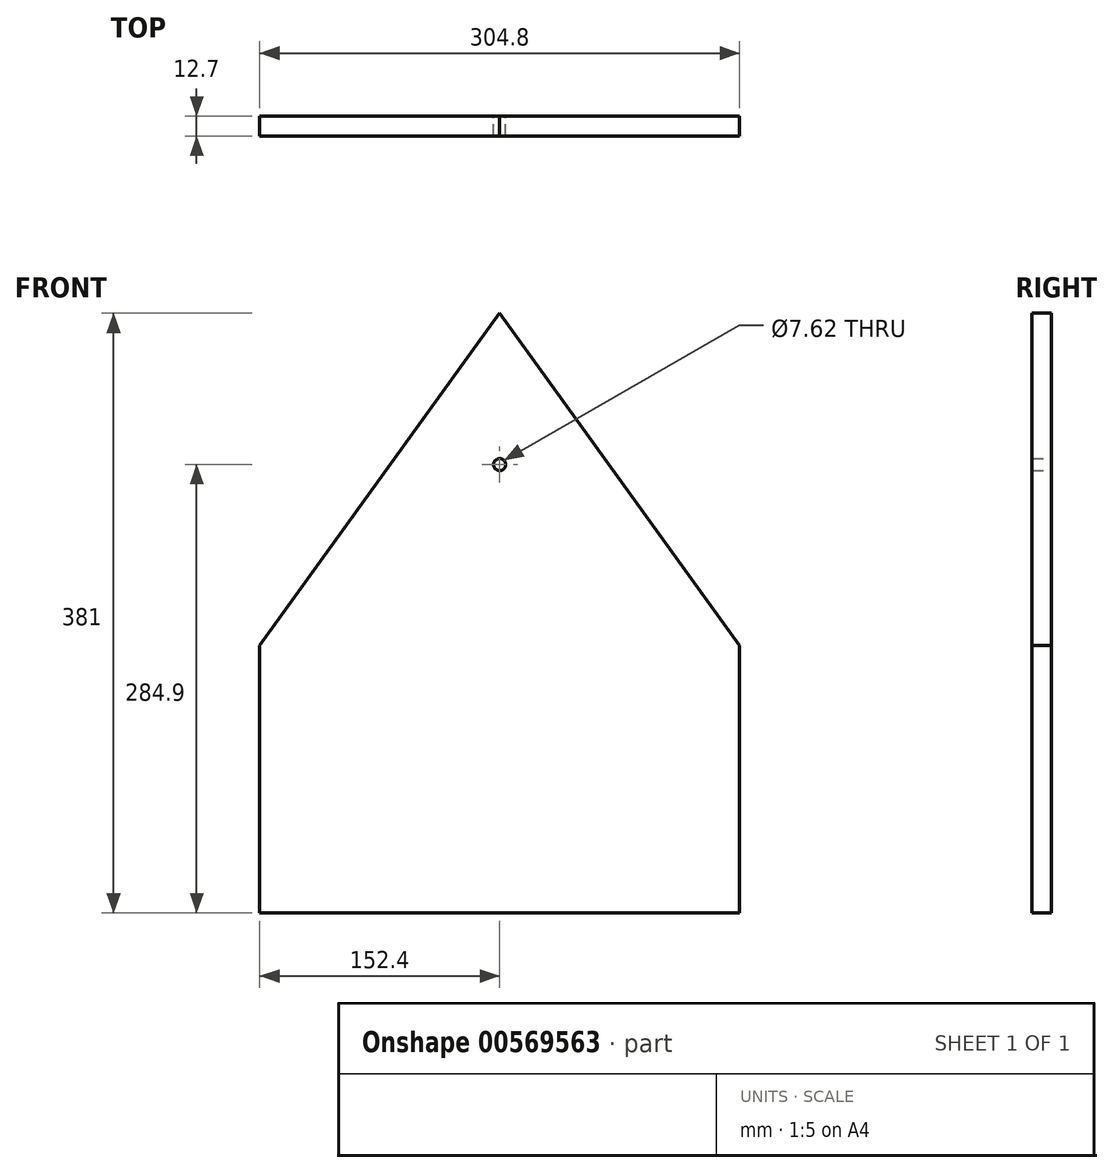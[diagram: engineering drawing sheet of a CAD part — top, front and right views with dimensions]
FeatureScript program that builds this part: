
annotation { "Feature Type Name" : "Feature", "Feature Type Description" : "" }
export const myFeature = defineFeature(function(context is Context, id is Id, definition is map)
    precondition{}
    {
        {
            var Q0;
            Q0=qCreatedBy(makeId("Front.planeOp"),FACE);
            var sketch = newSketch(context, id + "F0", { "sketchPlane" : qUnion([Q0])});
            skLineSegment(sketch, "E0.bottom", {"start": v(152.4, 0) * mm, "end": v(-152.4, 0) * mm});
            skLineSegment(sketch, "E0.left", {"start": v(152.4, 0) * mm, "end": v(152.4, 170.1) * mm});
            skLineSegment(sketch, "E0.right", {"start": v(-152.4, 0) * mm, "end": v(-152.4, 170.1) * mm});
            skPoint(sketch, "E0.middle", {"position": v(0, 85.05) * mm});
            skLineSegment(sketch, "E1", {"start": v(-152.4, 170.1) * mm, "end": v(0, 381) * mm});
            skLineSegment(sketch, "E2", {"start": v(0, 381) * mm, "end": v(152.4, 170.1) * mm});
            skLineSegment(sketch, "E3", {"start": v(0, 0) * mm, "end": v(0, 407.3) * mm, "construction": true});
            skCircle(sketch, "E4", {"center": v(0, 284.9) * mm, "radius": 3.81 * mm});
            skSolve(sketch);
        }
        {
            var Q0;
            Q0=makeQuery(id+"F0.imprint","IMPRINT",FACE,{"disambiguationData":[TD([[makeQuery(id+"F0.imprint","IMPRINT",EDGE,{"derivedFrom":sQuery(id+"F0.wireOp",EDGE,"E0.bottom")}),-1.0]])]});
            extrude(context, id + "F1", {"entities" : qUnion([Q0]), "endBound" : BoundingType.SYMMETRIC, "depth" : 12.7 * mm, "offsetDistance" : 25.4 * mm});
        }
    });
